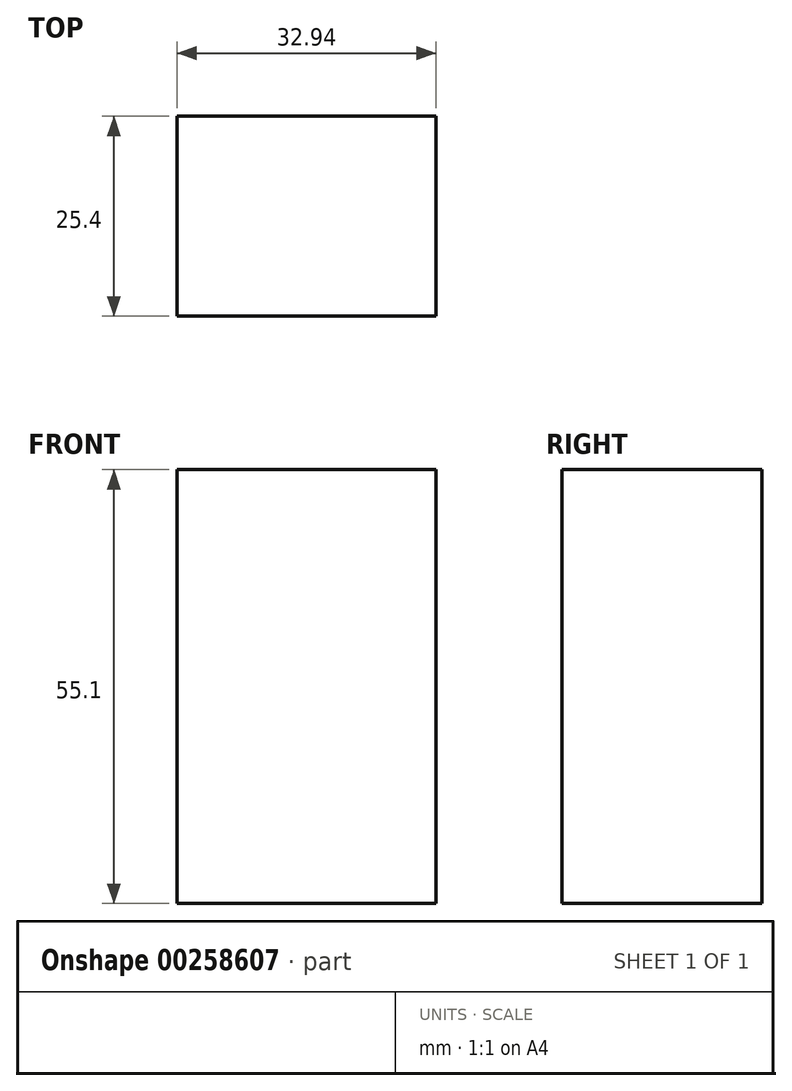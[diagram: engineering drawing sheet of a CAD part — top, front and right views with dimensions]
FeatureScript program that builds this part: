
annotation { "Feature Type Name" : "Feature", "Feature Type Description" : "" }
export const myFeature = defineFeature(function(context is Context, id is Id, definition is map)
    precondition{}
    {
        {
            var Q0;
            Q0=qCreatedBy(makeId("Front.planeOp"),FACE);
            var sketch = newSketch(context, id + "F0", { "sketchPlane" : qUnion([Q0])});
            skLineSegment(sketch, "E0.bottom", {"start": v(35.2, 0) * mm, "end": v(44.73, 0) * mm});
            skLineSegment(sketch, "E0.top", {"start": v(35.2, -42.53) * mm, "end": v(44.73, -42.53) * mm});
            skLineSegment(sketch, "E0.left", {"start": v(35.2, 0) * mm, "end": v(35.2, -42.53) * mm});
            skLineSegment(sketch, "E0.right", {"start": v(44.73, 0) * mm, "end": v(44.73, -42.53) * mm});
            skLineSegment(sketch, "E1.bottom", {"start": v(15.8, 35.94) * mm, "end": v(0, 35.94) * mm});
            skLineSegment(sketch, "E1.top", {"start": v(15.8, 31.4) * mm, "end": v(0, 31.4) * mm});
            skLineSegment(sketch, "E1.left", {"start": v(15.8, 35.94) * mm, "end": v(15.8, 31.4) * mm});
            skLineSegment(sketch, "E1.right", {"start": v(0, 35.94) * mm, "end": v(0, 31.4) * mm});
            skLineSegment(sketch, "E2.bottom", {"start": v(26.38, 21.38) * mm, "end": v(-6.56, 21.38) * mm});
            skLineSegment(sketch, "E2.top", {"start": v(26.38, -33.72) * mm, "end": v(-6.56, -33.72) * mm});
            skLineSegment(sketch, "E2.left", {"start": v(26.38, 21.38) * mm, "end": v(26.38, -33.72) * mm});
            skLineSegment(sketch, "E2.right", {"start": v(-6.56, 21.38) * mm, "end": v(-6.56, -33.72) * mm});
            skSolve(sketch);
        }
        {
            var Q0;
            Q0=makeQuery(id+"F0.imprint","IMPRINT",FACE,{"disambiguationData":[TD([[makeQuery(id+"F0.imprint","IMPRINT",EDGE,{"derivedFrom":sQuery(id+"F0.wireOp",EDGE,"E2.bottom")}),1.0]])]});
            var Q1;
            Q1=makeQuery(id+"F0.imprint","IMPRINT",FACE,{"disambiguationData":[TD([[makeQuery(id+"F0.imprint","IMPRINT",EDGE,{"derivedFrom":sQuery(id+"F0.wireOp",EDGE,"E2.bottom")}),1.0]])]});
            extrude(context, id + "F1", {"entities" : qUnion([Q0, Q1]), "depth" : 25.4 * mm});
        }
        {
            var Q0;
            Q0=makeQuery(id+"F0.imprint","IMPRINT",FACE,{"disambiguationData":[TD([[makeQuery(id+"F0.imprint","IMPRINT",EDGE,{"derivedFrom":sQuery(id+"F0.wireOp",EDGE,"E2.bottom")}),1.0]])]});
            var Q1;
            Q1=makeQuery(id+"F0.imprint","IMPRINT",FACE,{"disambiguationData":[TD([[makeQuery(id+"F0.imprint","IMPRINT",EDGE,{"derivedFrom":sQuery(id+"F0.wireOp",EDGE,"E2.bottom")}),1.0]])]});
            var Q2;
            Q2=makeQuery(id+"F0.imprint","IMPRINT",FACE,{"disambiguationData":[TD([[makeQuery(id+"F0.imprint","IMPRINT",EDGE,{"derivedFrom":sQuery(id+"F0.wireOp",EDGE,"E2.bottom")}),1.0]])]});
            var Q3;
            Q3=makeQuery(id+"F0.imprint","IMPRINT",FACE,{"disambiguationData":[TD([[makeQuery(id+"F0.imprint","IMPRINT",EDGE,{"derivedFrom":sQuery(id+"F0.wireOp",EDGE,"E2.bottom")}),1.0]])]});
            extrude(context, id + "F2", {"entities" : qUnion([Q0, Q1, Q2, Q3]), "operationType" : NewBodyOperationType.ADD, "depth" : 25.4 * mm});
        }
    });
